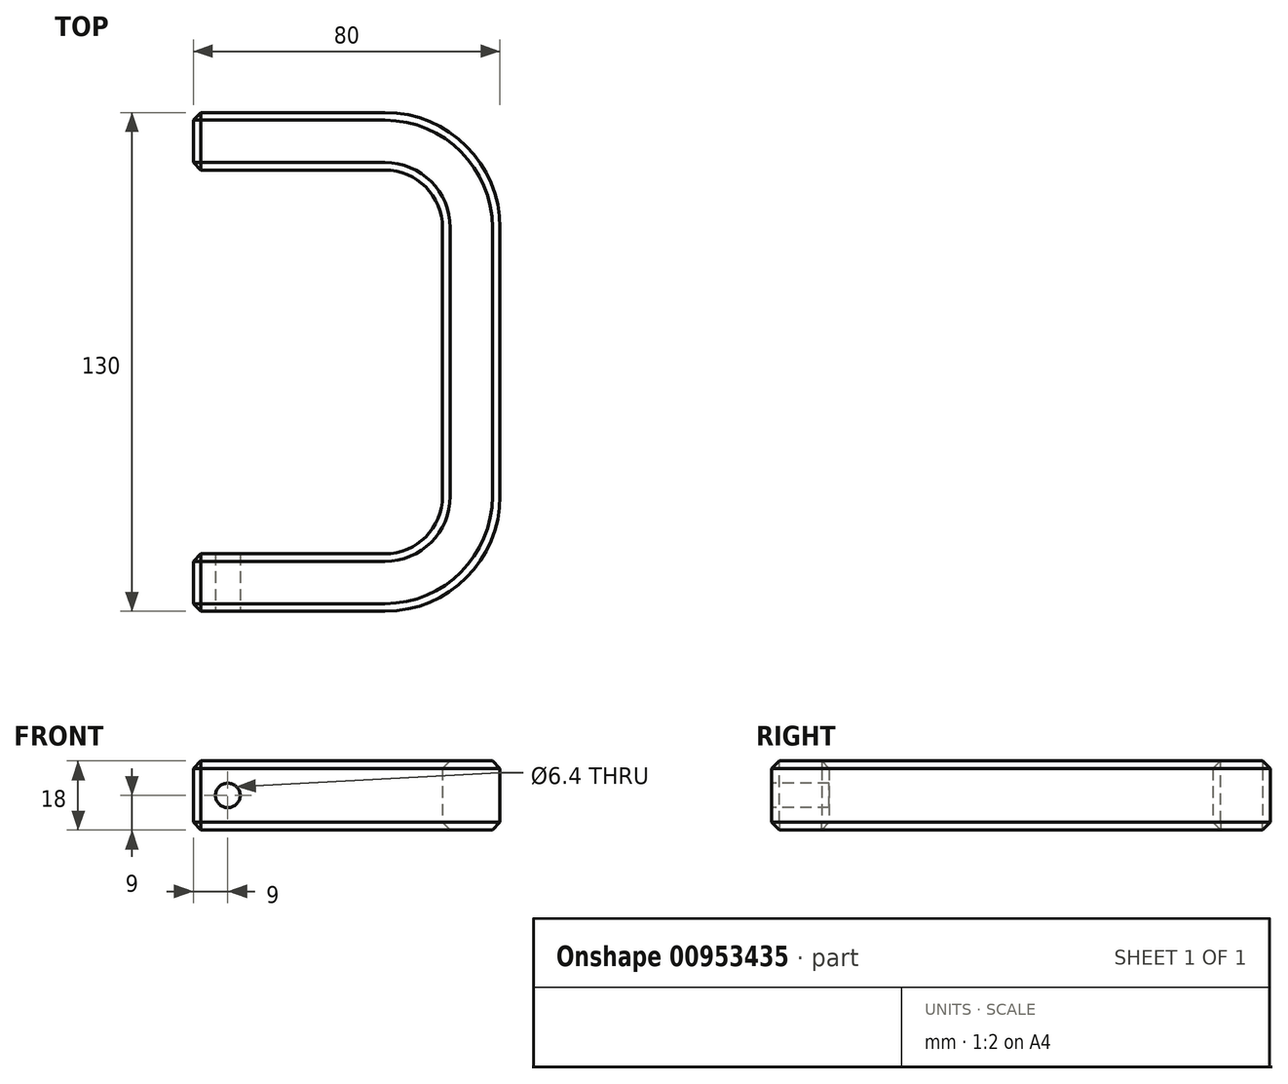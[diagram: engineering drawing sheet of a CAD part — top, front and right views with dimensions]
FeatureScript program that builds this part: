
annotation { "Feature Type Name" : "Feature", "Feature Type Description" : "" }
export const myFeature = defineFeature(function(context is Context, id is Id, definition is map)
    precondition{}
    {
        {
            var Q0;
            Q0=qCreatedBy(makeId("Top.planeOp"),FACE);
            var sketch = newSketch(context, id + "F0", { "sketchPlane" : qUnion([Q0])});
            skLineSegment(sketch, "E0", {"start": v(-9, 0) * mm, "end": v(41, 0) * mm});
            skArc(sketch, "E1", {"start": v(41, 0) * mm, "mid": v(51.6, 4.4) * mm, "end": v(56, 15) * mm});
            skLineSegment(sketch, "E2", {"start": v(56, 15) * mm, "end": v(56, 85) * mm});
            skArc(sketch, "E3", {"start": v(56, 85) * mm, "mid": v(51.6, 95.6) * mm, "end": v(41, 100) * mm});
            skLineSegment(sketch, "E4", {"start": v(41, 100) * mm, "end": v(-9, 100) * mm});
            skLineSegment(sketch, "E5", {"start": v(-9, 100) * mm, "end": v(-9, 115) * mm});
            skLineSegment(sketch, "E6", {"start": v(-9, 115) * mm, "end": v(41, 115) * mm});
            skLineSegment(sketch, "E7", {"start": v(71, 85) * mm, "end": v(71, 15) * mm});
            skLineSegment(sketch, "E8", {"start": v(41, -15) * mm, "end": v(-9, -15) * mm});
            skLineSegment(sketch, "E9", {"start": v(-9, -15) * mm, "end": v(-9, 0) * mm});
            skArc(sketch, "E10", {"start": v(41, 115) * mm, "mid": v(62.21, 106.21) * mm, "end": v(71, 85) * mm});
            skArc(sketch, "E11", {"start": v(41, -15) * mm, "mid": v(62.21, -6.21) * mm, "end": v(71, 15) * mm});
            skLineSegment(sketch, "E12", {"start": v(0, 0) * mm, "end": v(0, -15) * mm});
            skLineSegment(sketch, "E13", {"start": v(3.2, -15) * mm, "end": v(3.2, 0) * mm});
            skSolve(sketch);
        }
        {
            var Q0;
            {var subQ0=sQuery(id+"F0.wireOp",EDGE,"E5");Q0=makeQuery(id+"F0.imprint","IMPRINT",FACE,{"disambiguationData":[TD([[makeQuery(id+"F0.imprint","IMPRINT",EDGE,{"derivedFrom":subQ0}),-1.0]])]});}
            var Q1;
            {var subQ0=sQuery(id+"F0.wireOp",EDGE,"DthNqOgE-Gk1m-5kka-hVya-dyvI0kj7Sg4n");var subQ1=sQuery(id+"F0.wireOp",EDGE,"E4");var subQ2=makeQuery(id+"F0.imprint","INTERSECT",VERTEX,{"derivedFrom":[subQ1,subQ0]});Q1=makeQuery(id+"F0.imprint","IMPRINT",FACE,{"disambiguationData":[TD([[makeQuery(id+"F0.imprint","IMPRINT",EDGE,{"disambiguationData":[TD([[subQ2,1.0]])],"derivedFrom":subQ1}),-1.0]])]});}
            var Q2;
            {var subQ8=sQuery(id+"F0.wireOp",EDGE,"E1");Q2=makeQuery(id+"F0.imprint","IMPRINT",FACE,{"disambiguationData":[TD([[makeQuery(id+"F0.imprint","IMPRINT",EDGE,{"derivedFrom":subQ8}),-1.0]])]});}
            var Q3;
            {var subQ0=sQuery(id+"F0.wireOp",EDGE,"DthNqOgE-Gk1m-5kka-hVya-dyvI0kj7Sg4n");var subQ1=sQuery(id+"F0.wireOp",EDGE,"E0");var subQ2=makeQuery(id+"F0.imprint","INTERSECT",VERTEX,{"derivedFrom":[subQ1,subQ0]});Q3=makeQuery(id+"F0.imprint","IMPRINT",FACE,{"disambiguationData":[TD([[makeQuery(id+"F0.imprint","IMPRINT",EDGE,{"disambiguationData":[TD([[subQ2,-1.0]])],"derivedFrom":subQ1}),-1.0]])]});}
            var Q4;
            {var subQ0=sQuery(id+"F0.wireOp",EDGE,"E9");Q4=makeQuery(id+"F0.imprint","IMPRINT",FACE,{"disambiguationData":[TD([[makeQuery(id+"F0.imprint","IMPRINT",EDGE,{"derivedFrom":subQ0}),-1.0]])]});}
            var Q5;
            {var subQ0=sQuery(id+"F0.wireOp",EDGE,"i5MjP1mj-t0D3-PnyY-Cecg-qhch5Xo7VqnF");var subQ1=sQuery(id+"F0.wireOp",EDGE,"E4");var subQ2=makeQuery(id+"F0.imprint","INTERSECT",VERTEX,{"derivedFrom":[subQ1,subQ0]});Q5=makeQuery(id+"F0.imprint","IMPRINT",FACE,{"disambiguationData":[TD([[makeQuery(id+"F0.imprint","IMPRINT",EDGE,{"disambiguationData":[TD([[subQ2,-1.0]])],"derivedFrom":subQ1}),-1.0]])]});}
            var Q6;
            {var subQ0=sQuery(id+"F0.wireOp",EDGE,"e4gqwks8-qUmj-GK7P-ncf1-rGkQtQW7TUye");var subQ1=sQuery(id+"F0.wireOp",EDGE,"E0");var subQ2=makeQuery(id+"F0.imprint","INTERSECT",VERTEX,{"derivedFrom":[subQ1,subQ0]});Q6=makeQuery(id+"F0.imprint","IMPRINT",FACE,{"disambiguationData":[TD([[makeQuery(id+"F0.imprint","IMPRINT",EDGE,{"disambiguationData":[TD([[subQ2,-1.0]])],"derivedFrom":subQ1}),-1.0]])]});}
            extrude(context, id + "F1", {"entities" : qUnion([Q0, Q1, Q2, Q3, Q4, Q5, Q6]), "endBound" : BoundingType.SYMMETRIC, "depth" : 18 * mm, "offsetDistance" : 25 * mm});
        }
        {
            var Q0;
            {var subQ0=sQuery(id+"F0.wireOp",EDGE,"E12");Q0=makeQuery(id+"F0.imprint","IMPRINT",FACE,{"disambiguationData":[TD([[makeQuery(id+"F0.imprint","IMPRINT",EDGE,{"derivedFrom":subQ0}),1.0]])]});}
            var Q1;
            Q1=sQuery(id+"F0.wireOp",EDGE,"E12");
            revolve(context, id + "F2", {"operationType" : NewBodyOperationType.REMOVE, "surfaceOperationType" : NewSurfaceOperationType.NEW, "entities" : qUnion([Q0]), "axis" : qUnion([Q1]), "revolveType" : RevolveType.FULL, "oppositeDirection" : true});
        }
        {
            var Q0;
            Q0=makeQuery(id+"F1.opExtrude","CAP_FACE",FACE,{"disambiguationData":[OSD([sQuery(id+"F0.wireOp",EDGE,"E0"),sQuery(id+"F0.wireOp",EDGE,"E1"),sQuery(id+"F0.wireOp",EDGE,"E2"),sQuery(id+"F0.wireOp",EDGE,"E3"),sQuery(id+"F0.wireOp",EDGE,"E4"),sQuery(id+"F0.wireOp",EDGE,"E5"),sQuery(id+"F0.wireOp",EDGE,"E6"),sQuery(id+"F0.wireOp",EDGE,"E7"),sQuery(id+"F0.wireOp",EDGE,"E8"),sQuery(id+"F0.wireOp",EDGE,"E9"),sQuery(id+"F0.wireOp",EDGE,"E10"),sQuery(id+"F0.wireOp",EDGE,"E11")])],"isStart":false});
            var Q1;
            Q1=makeQuery(id+"F1.opExtrude","CAP_FACE",FACE,{"disambiguationData":[OSD([sQuery(id+"F0.wireOp",EDGE,"E0"),sQuery(id+"F0.wireOp",EDGE,"E1"),sQuery(id+"F0.wireOp",EDGE,"E2"),sQuery(id+"F0.wireOp",EDGE,"E3"),sQuery(id+"F0.wireOp",EDGE,"E4"),sQuery(id+"F0.wireOp",EDGE,"E5"),sQuery(id+"F0.wireOp",EDGE,"E6"),sQuery(id+"F0.wireOp",EDGE,"E7"),sQuery(id+"F0.wireOp",EDGE,"E8"),sQuery(id+"F0.wireOp",EDGE,"E9"),sQuery(id+"F0.wireOp",EDGE,"E10"),sQuery(id+"F0.wireOp",EDGE,"E11")])],"isStart":true});
            var Q2;
            Q2=makeQuery(id+"F1.opExtrude","SWEPT_FACE",FACE,{"disambiguationData":[OSD([sQuery(id+"F0.wireOp",EDGE,"E9")])]});
            var Q3;
            Q3=makeQuery(id+"F1.opExtrude","SWEPT_FACE",FACE,{"disambiguationData":[OSD([sQuery(id+"F0.wireOp",EDGE,"E5")])]});
            var Q4;
            Q4=makeQuery(id+"F2.boolean.opBoolean","COPY",EDGE,{"derivedFrom":makeQuery(id+"F2.opRevolve","SWEPT_EDGE",EDGE,{"disambiguationData":[OSD([sQuery(id+"F0.wireOp",EDGE,"E8"),sQuery(id+"F0.wireOp",EDGE,"E13")])]})});
            var Q5;
            Q5=makeQuery(id+"F2.boolean.opBoolean","COPY",EDGE,{"derivedFrom":makeQuery(id+"F2.opRevolve","SWEPT_EDGE",EDGE,{"disambiguationData":[OSD([sQuery(id+"F0.wireOp",EDGE,"E0"),sQuery(id+"F0.wireOp",EDGE,"E13")])]})});
            chamfer(context, id + "F3", {"entities" : qUnion([Q0, Q1, Q2, Q3, Q4, Q5]), "width" : 2 * mm, "tangentPropagation" : true});
        }
    });
